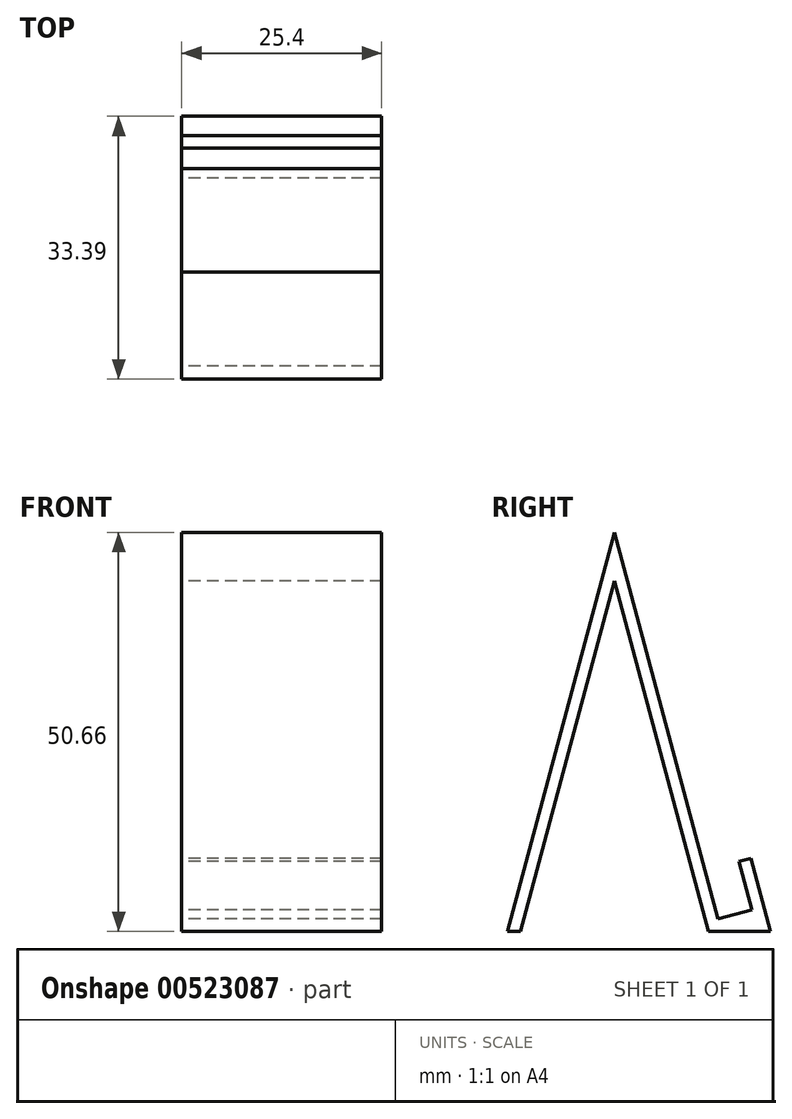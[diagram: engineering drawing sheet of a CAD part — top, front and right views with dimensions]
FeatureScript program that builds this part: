
annotation { "Feature Type Name" : "Feature", "Feature Type Description" : "" }
export const myFeature = defineFeature(function(context is Context, id is Id, definition is map)
    precondition{}
    {
        {
            var Q0;
            Q0=qCreatedBy(makeId("Right.planeOp"),FACE);
            var sketch = newSketch(context, id + "F0", { "sketchPlane" : qUnion([Q0])});
            skLineSegment(sketch, "E0", {"start": v(0, 0) * mm, "end": v(-11.93, 44.52) * mm});
            skLineSegment(sketch, "E1", {"start": v(-11.93, 44.52) * mm, "end": v(-23.86, 0) * mm});
            skLineSegment(sketch, "E2", {"start": v(-11.93, 44.52) * mm, "end": v(-11.93, 0) * mm, "construction": true});
            skLineSegment(sketch, "E3", {"start": v(0, 0) * mm, "end": v(7.89, 0) * mm});
            skLineSegment(sketch, "E4", {"start": v(7.89, 0) * mm, "end": v(5.4, 9.28) * mm});
            skLineSegment(sketch, "E5", {"start": v(5.4, 9.28) * mm, "end": v(3.87, 8.87) * mm});
            skLineSegment(sketch, "E6", {"start": v(3.87, 8.87) * mm, "end": v(5.51, 2.74) * mm});
            skLineSegment(sketch, "E7", {"start": v(5.51, 2.74) * mm, "end": v(1.22, 1.59) * mm});
            skLineSegment(sketch, "E8", {"start": v(1.22, 1.59) * mm, "end": v(-11.93, 50.66) * mm});
            skLineSegment(sketch, "E9", {"start": v(-11.93, 50.66) * mm, "end": v(-25.5, 0) * mm});
            skLineSegment(sketch, "E10", {"start": v(-25.5, 0) * mm, "end": v(-23.86, 0) * mm});
            skSolve(sketch);
        }
        {
            var Q0;
            Q0 = qSketchRegion(id + "F0", true);
            extrude(context, id + "F1", {"entities" : qUnion([Q0]), "depth" : 25.4 * mm, "offsetDistance" : 25.4 * mm});
        }
    });
